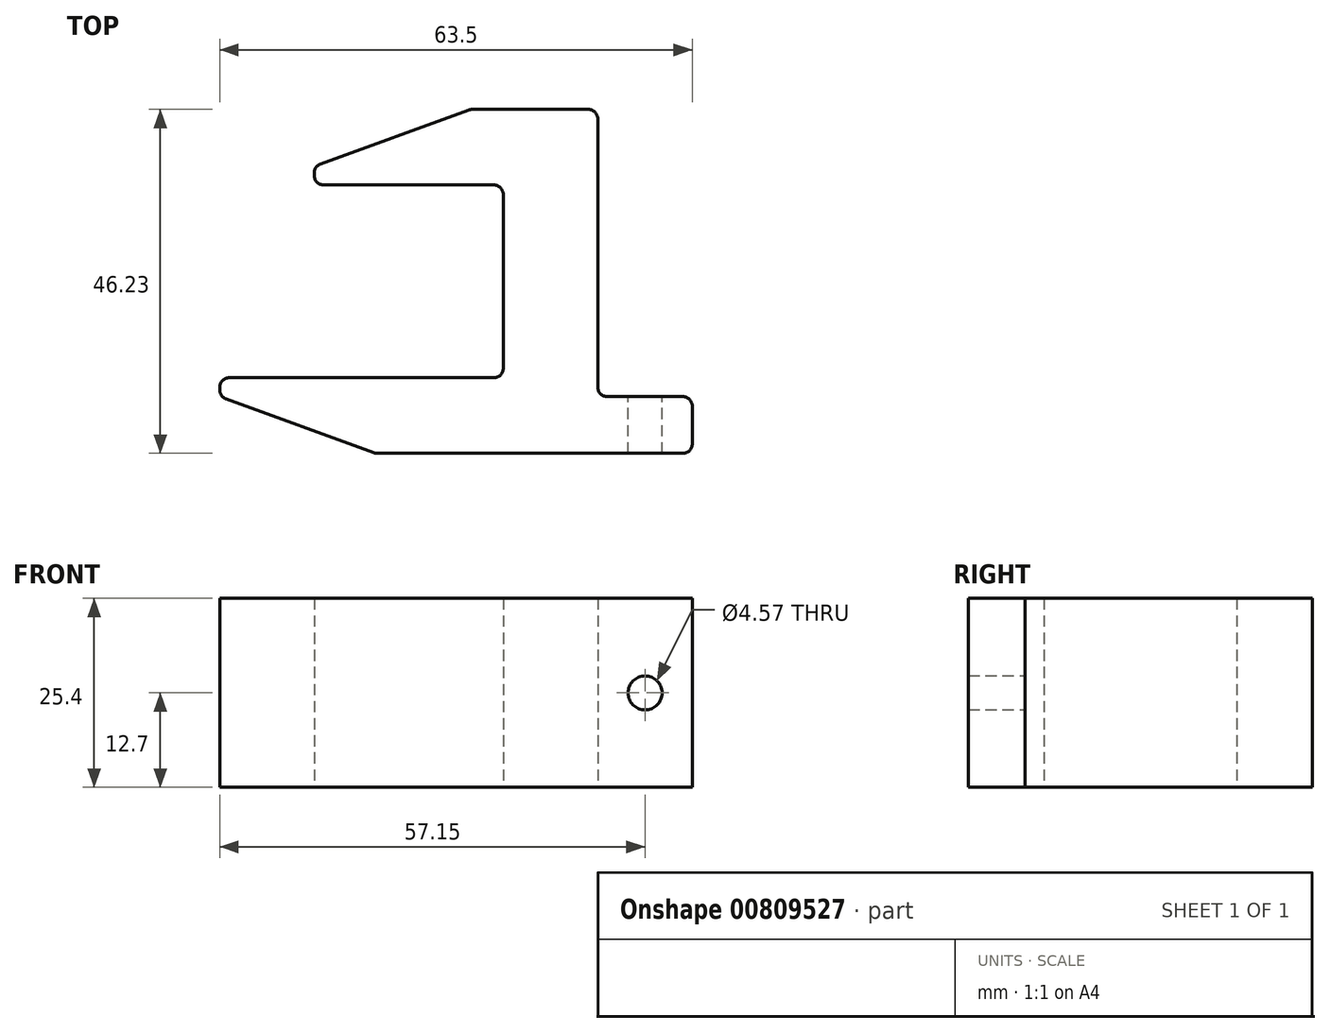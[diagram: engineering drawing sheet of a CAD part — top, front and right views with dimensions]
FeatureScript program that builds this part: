
annotation { "Feature Type Name" : "Feature", "Feature Type Description" : "" }
export const myFeature = defineFeature(function(context is Context, id is Id, definition is map)
    precondition{}
    {
        {
            var Q0;
            Q0=qCreatedBy(makeId("Top.planeOp"),FACE);
            var sketch = newSketch(context, id + "F0", { "sketchPlane" : qUnion([Q0])});
            skLineSegment(sketch, "E0", {"start": v(-3.81, 2.54) * mm, "end": v(-44.88, 2.54) * mm});
            skLineSegment(sketch, "E1", {"start": v(-66.04, 11.05) * mm, "end": v(-66.04, 11.43) * mm});
            skLineSegment(sketch, "E2", {"start": v(-64.77, 12.7) * mm, "end": v(-29.2, 12.7) * mm});
            skLineSegment(sketch, "E3", {"start": v(-27.94, 13.97) * mm, "end": v(-27.94, 37.34) * mm});
            skLineSegment(sketch, "E4", {"start": v(-29.21, 38.6) * mm, "end": v(-52.07, 38.6) * mm});
            skLineSegment(sketch, "E5", {"start": v(-32.18, 48.77) * mm, "end": v(-15.24, 48.77) * mm});
            skLineSegment(sketch, "E6", {"start": v(-2.54, 10.16) * mm, "end": v(-2.54, 3.81) * mm});
            skLineSegment(sketch, "E7", {"start": v(-53.34, 39.88) * mm, "end": v(-53.34, 40.26) * mm});
            skLineSegment(sketch, "E8", {"start": v(-52.5, 41.45) * mm, "end": v(-32.61, 48.7) * mm});
            skLineSegment(sketch, "E9", {"start": v(-65.2, 9.86) * mm, "end": v(-45.31, 2.62) * mm});
            skPoint(sketch, "E10.visualSharp", {"position": v(-53.34, 41.15) * mm});
            skArc(sketch, "E10.filletArc", {"start": v(-52.5, 41.45) * mm, "mid": v(-53.11, 40.99) * mm, "end": v(-53.34, 40.26) * mm});
            skPoint(sketch, "E11.visualSharp", {"position": v(-53.34, 38.6) * mm});
            skArc(sketch, "E11.filletArc", {"start": v(-53.34, 39.88) * mm, "mid": v(-52.97, 38.98) * mm, "end": v(-52.07, 38.6) * mm});
            skPoint(sketch, "E12.visualSharp", {"position": v(-66.04, 12.7) * mm});
            skArc(sketch, "E12.filletArc", {"start": v(-64.77, 12.7) * mm, "mid": v(-65.67, 12.33) * mm, "end": v(-66.04, 11.43) * mm});
            skPoint(sketch, "E13.visualSharp", {"position": v(-66.04, 10.16) * mm});
            skArc(sketch, "E13.filletArc", {"start": v(-66.04, 11.05) * mm, "mid": v(-65.81, 10.32) * mm, "end": v(-65.2, 9.86) * mm});
            skPoint(sketch, "E14.visualSharp", {"position": v(-45.1, 2.54) * mm});
            skArc(sketch, "E14.filletArc", {"start": v(-45.31, 2.62) * mm, "mid": v(-45.1, 2.56) * mm, "end": v(-44.88, 2.54) * mm});
            skPoint(sketch, "E15.visualSharp", {"position": v(-27.94, 12.7) * mm});
            skArc(sketch, "E15.filletArc", {"start": v(-29.2, 12.7) * mm, "mid": v(-28.31, 13.07) * mm, "end": v(-27.94, 13.97) * mm});
            skPoint(sketch, "E16.visualSharp", {"position": v(-27.94, 38.6) * mm});
            skArc(sketch, "E16.filletArc", {"start": v(-27.94, 37.34) * mm, "mid": v(-28.31, 38.24) * mm, "end": v(-29.21, 38.6) * mm});
            skPoint(sketch, "E17.visualSharp", {"position": v(-32.4, 48.77) * mm});
            skArc(sketch, "E17.filletArc", {"start": v(-32.18, 48.77) * mm, "mid": v(-32.4, 48.75) * mm, "end": v(-32.61, 48.7) * mm});
            skPoint(sketch, "E18.visualSharp", {"position": v(-2.54, 2.54) * mm});
            skArc(sketch, "E18.filletArc", {"start": v(-3.81, 2.54) * mm, "mid": v(-2.91, 2.91) * mm, "end": v(-2.54, 3.81) * mm});
            skLineSegment(sketch, "E19", {"start": v(-15.24, 48.77) * mm, "end": v(-15.24, 10.16) * mm});
            skLineSegment(sketch, "E20", {"start": v(-15.24, 10.16) * mm, "end": v(-2.54, 10.16) * mm});
            skSolve(sketch);
        }
        {
            var Q0;
            Q0 = qSketchRegion(id + "F0", true);
            extrude(context, id + "F1", {"entities" : qUnion([Q0]), "depth" : 25.4 * mm, "offsetDistance" : 25.4 * mm});
        }
        {
            var Q0;
            Q0=makeQuery(id+"F1.opExtrude","SWEPT_EDGE",EDGE,{"disambiguationData":[OSD([sQuery(id+"F0.wireOp",EDGE,"E19"),sQuery(id+"F0.wireOp",EDGE,"E20")])]});
            var Q1;
            Q1=makeQuery(id+"F1.opExtrude","SWEPT_EDGE",EDGE,{"disambiguationData":[OSD([sQuery(id+"F0.wireOp",EDGE,"E6"),sQuery(id+"F0.wireOp",EDGE,"E20")])]});
            var Q2;
            Q2=makeQuery(id+"F1.opExtrude","SWEPT_EDGE",EDGE,{"disambiguationData":[OSD([sQuery(id+"F0.wireOp",EDGE,"E5"),sQuery(id+"F0.wireOp",EDGE,"E19")])]});
            fillet(context, id + "F2", {"entities" : qUnion([Q0, Q1, Q2]), "radius" : 1.27 * mm, "tangentPropagation" : true, "allowEdgeOverflow" : false});
        }
        {
            var Q0;
            Q0=makeQuery(id+"F1.opExtrude","SWEPT_FACE",FACE,{"disambiguationData":[OSD([sQuery(id+"F0.wireOp",EDGE,"E20")])]});
            var sketch = newSketch(context, id + "F3", { "sketchPlane" : qUnion([Q0])});
            skCircle(sketch, "E21", {"center": v(8.89, 12.7) * mm, "radius": 2.29 * mm});
            skSolve(sketch);
        }
        {
            var Q0;
            Q0 = qSketchRegion(id + "F3", true);
            extrude(context, id + "F4", {"entities" : qUnion([Q0]), "operationType" : NewBodyOperationType.REMOVE, "endBound" : BoundingType.UP_TO_NEXT, "oppositeDirection" : true, "depth" : 25.4 * mm, "offsetDistance" : 25.4 * mm});
        }
    });
